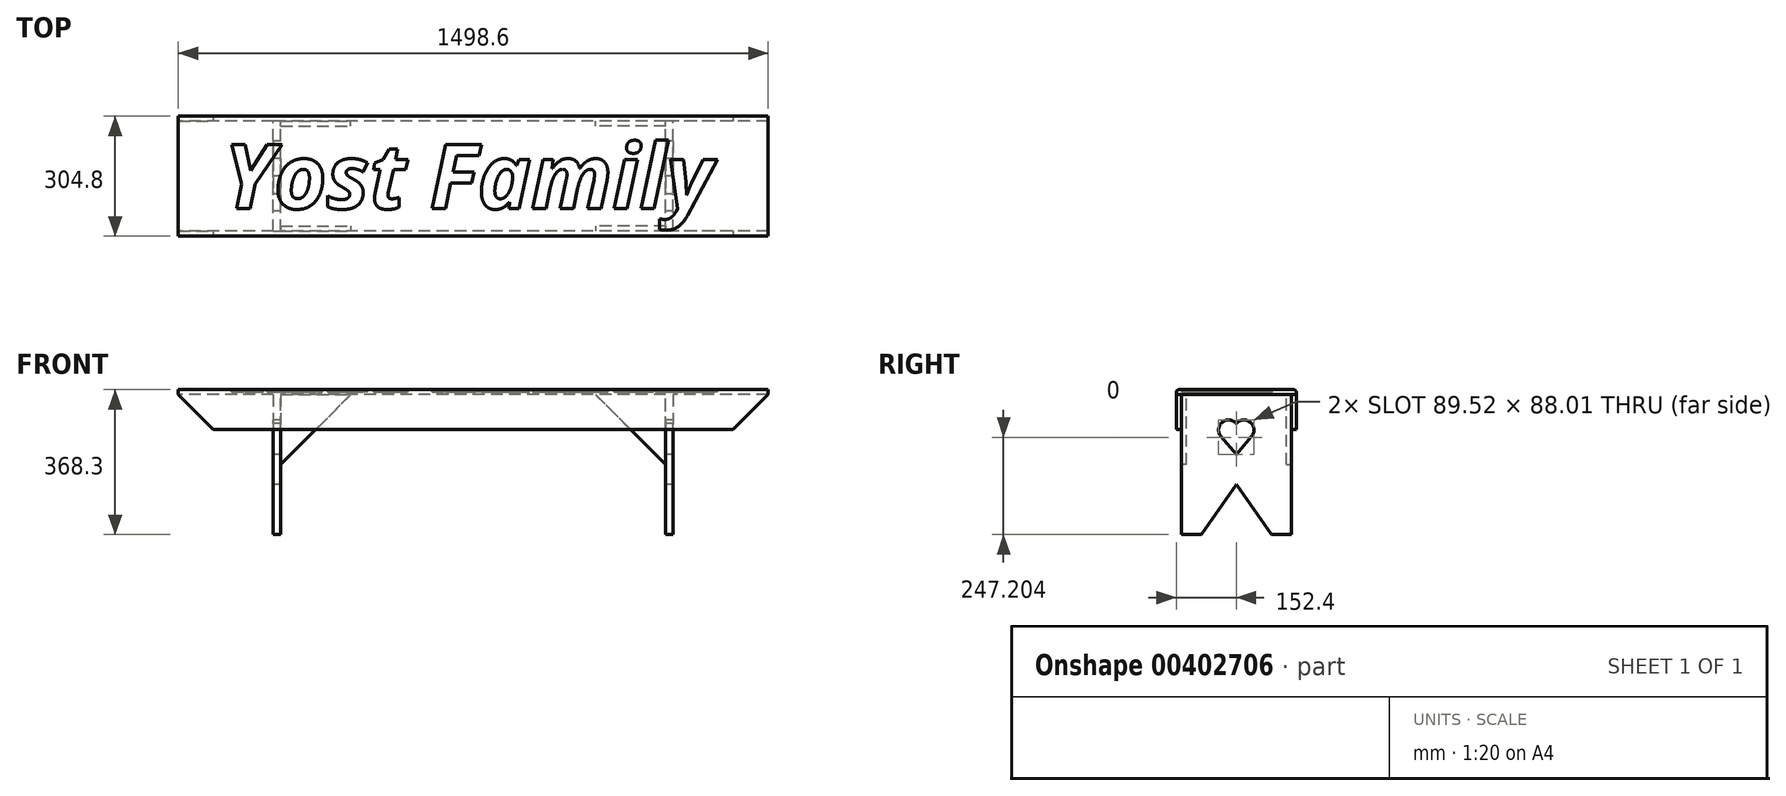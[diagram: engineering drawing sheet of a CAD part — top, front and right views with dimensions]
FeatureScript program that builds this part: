
annotation { "Feature Type Name" : "Feature", "Feature Type Description" : "" }
export const myFeature = defineFeature(function(context is Context, id is Id, definition is map)
    precondition{}
    {
        {
            var Q0;
            Q0=qCreatedBy(makeId("Front.planeOp"),FACE);
            var sketch = newSketch(context, id + "F0", { "sketchPlane" : qUnion([Q0])});
            skLineSegment(sketch, "E0", {"start": v(0, 0) * mm, "end": v(0, 152.4) * mm, "construction": true});
            skSolve(sketch);
        }
        {
            var Q0;
            Q0=qCreatedBy(makeId("Right.planeOp"),FACE);
            var sketch = newSketch(context, id + "F1", { "sketchPlane" : qUnion([Q0])});
            skLineSegment(sketch, "E1.top", {"start": v(152.4, 50.8) * mm, "end": v(-152.4, 50.8) * mm});
            skLineSegment(sketch, "E1.left", {"start": v(152.4, -50.8) * mm, "end": v(152.4, 50.8) * mm});
            skLineSegment(sketch, "E1.right", {"start": v(-152.4, -50.8) * mm, "end": v(-152.4, 50.8) * mm});
            skPoint(sketch, "E1.middle", {"position": v(0, 0) * mm});
            skLineSegment(sketch, "E2.0", {"start": v(139.7, -50.8) * mm, "end": v(139.7, 38.1) * mm});
            skLineSegment(sketch, "E2.1", {"start": v(139.7, 38.1) * mm, "end": v(-139.7, 38.1) * mm});
            skLineSegment(sketch, "E2.2", {"start": v(-139.7, -50.8) * mm, "end": v(-139.7, 38.1) * mm});
            skLineSegment(sketch, "E3", {"start": v(-139.7, -50.8) * mm, "end": v(-152.4, -50.8) * mm});
            skLineSegment(sketch, "E4", {"start": v(152.4, -50.8) * mm, "end": v(139.7, -50.8) * mm});
            skSolve(sketch);
        }
        {
            var Q0;
            Q0 = qSketchRegion(id + "F1", true);
            extrude(context, id + "F2", {"entities" : qUnion([Q0]), "depth" : 762 * mm, "hasSecondDirection" : true, "secondDirectionOppositeDirection" : true, "secondDirectionDepth" : 762 * mm});
        }
        {
            var Q0;
            Q0=makeQuery(id+"F2.opExtrude","SWEPT_FACE",FACE,{"disambiguationData":[OSD([sQuery(id+"F1.wireOp",EDGE,"E1.right")])]});
            var sketch = newSketch(context, id + "F3", { "sketchPlane" : qUnion([Q0])});
            skLineSegment(sketch, "E5", {"start": v(-762, 50.8) * mm, "end": v(-660.4, -50.8) * mm});
            skLineSegment(sketch, "E6.MirrorCS", {"start": v(762, 50.8) * mm, "end": v(660.4, -50.8) * mm});
            skSolve(sketch);
        }
        {
            var Q0;
            {var subQ0=sQuery(id+"F3.wireOp",EDGE,"E5");Q0=makeQuery(id+"F3.imprint","IMPRINT",FACE,{"disambiguationData":[TD([[makeQuery(id+"F3.imprint","IMPRINT",EDGE,{"derivedFrom":subQ0}),-1.0]])]});}
            var Q1;
            {var subQ0=sQuery(id+"F3.wireOp",EDGE,"E6.MirrorCS");Q1=makeQuery(id+"F3.imprint","IMPRINT",FACE,{"disambiguationData":[TD([[makeQuery(id+"F3.imprint","IMPRINT",EDGE,{"derivedFrom":subQ0}),1.0]])]});}
            extrude(context, id + "F4", {"entities" : qUnion([Q0, Q1]), "operationType" : NewBodyOperationType.REMOVE, "endBound" : BoundingType.THROUGH_ALL, "oppositeDirection" : true, "depth" : 25.4 * mm});
        }
        {
            var Q0;
            Q0=makeQuery(id+"F2.opExtrude","SWEPT_FACE",FACE,{"disambiguationData":[OSD([sQuery(id+"F1.wireOp",EDGE,"E2.0")])]});
            var sketch = newSketch(context, id + "F5", { "sketchPlane" : qUnion([Q0])});
            skLineSegment(sketch, "E7.bottom", {"start": v(-508, 38.1) * mm, "end": v(-488.95, 38.1) * mm});
            skLineSegment(sketch, "E7.top", {"start": v(-508, -317.5) * mm, "end": v(-488.95, -317.5) * mm});
            skLineSegment(sketch, "E7.left", {"start": v(-508, 38.1) * mm, "end": v(-508, -317.5) * mm});
            skLineSegment(sketch, "E7.right", {"start": v(-488.95, 38.1) * mm, "end": v(-488.95, -317.5) * mm});
            skSolve(sketch);
        }
        {
            var Q0;
            Q0 = qSketchRegion(id + "F5", true);
            extrude(context, id + "F6", {"entities" : qUnion([Q0]), "depth" : 279.4 * mm});
        }
        {
            var Q0;
            Q0=makeQuery(id+"F6.opExtrude","SWEPT_BODY",BODY,{"disambiguationData":[OSD([sQuery(id+"F5.wireOp",EDGE,"E7.bottom"),sQuery(id+"F5.wireOp",EDGE,"E7.top"),sQuery(id+"F5.wireOp",EDGE,"E7.left"),sQuery(id+"F5.wireOp",EDGE,"E7.right")])]});
            var Q1;
            Q1=qCreatedBy(makeId("Right.planeOp"),FACE);
            mirror(context, id + "F7", {"operationType" : NewBodyOperationType.ADD, "entities" : qUnion([Q0]), "mirrorPlane" : qUnion([Q1])});
        }
        {
            var Q0;
            Q0=makeQuery(id+"F6.opExtrude","SWEPT_FACE",FACE,{"disambiguationData":[OSD([sQuery(id+"F5.wireOp",EDGE,"E7.left")])]});
            var sketch = newSketch(context, id + "F8", { "sketchPlane" : qUnion([Q0])});
            skLineSegment(sketch, "E8", {"start": v(-88.9, -317.5) * mm, "end": v(0, -190.5) * mm});
            skPoint(sketch, "E8.endSnap0", {"position": v(0, -317.5) * mm});
            skLineSegment(sketch, "E9.MirrorCS", {"start": v(88.9, -317.5) * mm, "end": v(0, -190.5) * mm});
            skLineSegment(sketch, "E10", {"start": v(0, -114.3) * mm, "end": v(38.92, -67.92) * mm});
            skArc(sketch, "E11", {"start": v(38.92, -67.92) * mm, "mid": v(35.78, -32.14) * mm, "end": v(0, -35.27) * mm});
            skPoint(sketch, "E11.second.point", {"position": v(9.72, -28.14) * mm});
            skPoint(sketch, "E11.third.point", {"position": v(0, -67.92) * mm});
            skArc(sketch, "E12.MirrorC", {"start": v(-38.92, -67.92) * mm, "mid": v(-35.78, -32.14) * mm, "end": v(0, -35.27) * mm});
            skLineSegment(sketch, "E13.MirrorCS", {"start": v(0, -114.3) * mm, "end": v(-38.92, -67.92) * mm});
            skSolve(sketch);
        }
        {
            var Q0;
            Q0 = qSketchRegion(id + "F8", true);
            var Q1;
            {var subQ0=sQuery(id+"F8.wireOp",EDGE,"E8");Q1=makeQuery(id+"F8.imprint","IMPRINT",FACE,{"disambiguationData":[TD([[makeQuery(id+"F8.imprint","IMPRINT",EDGE,{"derivedFrom":subQ0}),-1.0]])]});}
            extrude(context, id + "F9", {"entities" : qUnion([Q0, Q1]), "operationType" : NewBodyOperationType.REMOVE, "endBound" : BoundingType.THROUGH_ALL, "oppositeDirection" : true, "depth" : 25.4 * mm});
        }
        {
            var Q0;
            {var subQ0=sQuery(id+"F1.wireOp",EDGE,"E1.top");Q0=makeQuery(id+"F4.boolean.opBoolean","MERGE",EDGE,{"derivedFrom":[makeQuery(id+"F2.opExtrude","CAP_EDGE",EDGE,{"disambiguationData":[OSD([subQ0])],"isStart":true}),makeQuery(id+"F4.opExtrude","SWEPT_EDGE",EDGE,{"disambiguationData":[OSD([subQ0,sQuery(id+"F1.wireOp",EDGE,"E1.right"),sQuery(id+"F3.wireOp",EDGE,"E5")])]})]});}
            var Q1;
            {var subQ0=sQuery(id+"F1.wireOp",EDGE,"E1.top");Q1=makeQuery(id+"F4.boolean.opBoolean","MERGE",EDGE,{"derivedFrom":[makeQuery(id+"F2.opExtrude","CAP_EDGE",EDGE,{"disambiguationData":[OSD([subQ0])],"isStart":false}),makeQuery(id+"F4.opExtrude","SWEPT_EDGE",EDGE,{"disambiguationData":[OSD([subQ0,sQuery(id+"F1.wireOp",EDGE,"E1.right"),sQuery(id+"F3.wireOp",EDGE,"E6.MirrorCS")])]})]});}
            chamfer(context, id + "F10", {"entities" : qUnion([Q0, Q1]), "chamferType" : ChamferType.OFFSET_ANGLE, "width" : 12.7 * mm, "oppositeDirection" : false, "angle" : 90 * degree, "tangentPropagation" : true});
        }
        {
            var Q0;
            Q0=makeQuery(id+"F2.opExtrude","SWEPT_EDGE",EDGE,{"disambiguationData":[OSD([sQuery(id+"F1.wireOp",EDGE,"E1.top"),sQuery(id+"F1.wireOp",EDGE,"E1.right")])]});
            var Q1;
            Q1=makeQuery(id+"F2.opExtrude","SWEPT_EDGE",EDGE,{"disambiguationData":[OSD([sQuery(id+"F1.wireOp",EDGE,"E1.top"),sQuery(id+"F1.wireOp",EDGE,"E1.left")])]});
            fillet(context, id + "F11", {"entities" : qUnion([Q0, Q1]), "radius" : 6.35 * mm, "tangentPropagation" : true, "allowEdgeOverflow" : false});
        }
        {
            var Q0;
            Q0=makeQuery(id+"F2.opExtrude","SWEPT_FACE",FACE,{"disambiguationData":[OSD([sQuery(id+"F1.wireOp",EDGE,"E1.top")])]});
            var sketch = newSketch(context, id + "F12", { "sketchPlane" : qUnion([Q0])});
            skText(sketch, "E14", { "text": "Yost Family", "fontName": "OpenSans-BoldItalic.ttf"});
            const initialGuessF12  = {"E14": [-0.635, -0.08236, 1, 0, 0.16472]};
            skSetInitialGuess(sketch, initialGuessF12);
            skSolve(sketch);
        }
        {
            var Q0;
            Q0 = qSketchRegion(id + "F12", true);
            extrude(context, id + "F13", {"entities" : qUnion([Q0]), "operationType" : NewBodyOperationType.REMOVE, "oppositeDirection" : true, "depth" : 6.35 * mm});
        }
        {
            var Q0;
            {var subQ0=sQuery(id+"F5.wireOp",EDGE,"E7.right");var subQ1=makeQuery(id+"F6.opExtrude","SWEPT_FACE",FACE,{"disambiguationData":[OSD([subQ0])]});Q0=makeQuery(id+"F7.boolean.opBoolean","SPLIT",FACE,{"disambiguationData":[TD([subQ1])],"derivedFrom":makeQuery(id+"F2.opExtrude","SWEPT_FACE",FACE,{"disambiguationData":[OSD([sQuery(id+"F1.wireOp",EDGE,"E2.2")])]})});}
            var sketch = newSketch(context, id + "F14", { "sketchPlane" : qUnion([Q0])});
            skLineSegment(sketch, "E15", {"start": v(-488.95, -139.7) * mm, "end": v(-311.15, 38.1) * mm});
            skLineSegment(sketch, "E16", {"start": v(-488.95, -139.7) * mm, "end": v(-488.95, 38.1) * mm});
            skLineSegment(sketch, "E17", {"start": v(-488.95, 38.1) * mm, "end": v(-311.15, 38.1) * mm});
            skSolve(sketch);
        }
        {
            var Q0;
            {var subQ0=sQuery(id+"F14.wireOp",EDGE,"E16");var subQ1=sQuery(id+"F14.wireOp",EDGE,"E15");var subQ2=makeQuery(id+"F14.imprint","INTERSECT",VERTEX,{"derivedFrom":[subQ1,subQ0]});Q0=makeQuery(id+"F14.imprint","IMPRINT",FACE,{"disambiguationData":[TD([[makeQuery(id+"F14.imprint","IMPRINT",EDGE,{"disambiguationData":[TD([[subQ2,-1.0]])],"derivedFrom":subQ1}),1.0]])]});}
            var Q1;
            {var subQ0=sQuery(id+"F14.wireOp",EDGE,"E17");Q1=makeQuery(id+"F14.imprint","IMPRINT",FACE,{"disambiguationData":[TD([[makeQuery(id+"F14.imprint","IMPRINT",EDGE,{"derivedFrom":subQ0}),-1.0]])]});}
            extrude(context, id + "F15", {"entities" : qUnion([Q0, Q1]), "depth" : 12.7 * mm});
        }
        {
            var Q0;
            Q0=makeQuery(id+"F15.opExtrude","SWEPT_BODY",BODY,{"disambiguationData":[OSD([sQuery(id+"F14.wireOp",EDGE,"E15"),sQuery(id+"F14.wireOp",EDGE,"E16"),sQuery(id+"F14.wireOp",EDGE,"E17")])]});
            var Q1;
            Q1=qCreatedBy(makeId("Front.planeOp"),FACE);
            mirror(context, id + "F16", {"entities" : qUnion([Q0]), "mirrorPlane" : qUnion([Q1])});
        }
        {
            var Q0;
            Q0=makeQuery(id+"F15.opExtrude","SWEPT_BODY",BODY,{"disambiguationData":[OSD([sQuery(id+"F14.wireOp",EDGE,"E15"),sQuery(id+"F14.wireOp",EDGE,"E16"),sQuery(id+"F14.wireOp",EDGE,"E17")])]});
            var Q1;
            Q1=makeQuery(id+"F16.opPattern","COPY",BODY,{"derivedFrom":makeQuery(id+"F15.opExtrude","SWEPT_BODY",BODY,{"disambiguationData":[OSD([sQuery(id+"F14.wireOp",EDGE,"E15"),sQuery(id+"F14.wireOp",EDGE,"E16"),sQuery(id+"F14.wireOp",EDGE,"E17")])]}),"instanceName":"1"});
            var Q2;
            Q2=qCreatedBy(makeId("Right.planeOp"),FACE);
            mirror(context, id + "F17", {"entities" : qUnion([Q0, Q1]), "mirrorPlane" : qUnion([Q2])});
        }
    });
